# Revit family: FR_MEADRAIN_DM_CITY_Basic
name_source: partatom
category: Allgemeines Modell
revit_build: Autodesk Revit 2018 (Build: 20170223_1515(x64)
units: mm (PartAtom-declared; Revit-internal decimal feet)

## family parameters
Beim Laden mit Abzugskörper schneiden = Ja
Bemaßung runder Anschluss = Durchmesser verwenden
Gemeinsam genutzt = Nein
Kann Basisbauteil für Bewehrung sein = Nein
Raumberechnungspunkt = Nein
Teiletyp = Normal

## types (3) — shared parameters
B_diamétre intérieure_Manchon = 180 mm  [stored 0.590551 ft]
Bauelement = Caniveaux de surface
Beschreibung = System universel de drainage en béton polymère classes de charges jusqu'à D400
Def classe de charge_caniveau = D400
Diamétre extérieure_Manchon_element de revision = 200 mm  [stored 0.656168 ft]
Elément de drainage adapté pour = Pour une utilisation en milieu urbain
Fiche technique produit = https://www.mea-group.com
Fondation_largeur = 200 mm  [stored 0.656168 ft]
Grille = Gussrost
Hersteller = MEA Bautechnik GmbH business unit MEA Water Management
Hersteller und Typ- Ausschreibender gleichwertig = comme MEA Bautechnik GmbH, modèle MEADRAIN S
IfcDescription = System universel de drainage en béton polymère classes de charges jusqu'à D400
IfcExportAs = IfcWasteTerminalType
IfcExportType = USERDEFINED
Lien pour les produit = https://www.mea-group.com
Longeur_Manchon_Avaloir = 194 mm
Longeur_Manchon_element de revision = 180 mm  [stored 0.590551 ft]
MEA Consignes de pose = einschl. Fundament und Ummantelung
Matériau de construction, lit de pose/fondation = conformément aux dessins et à la description du produits
Modell = MEADRAIN DM
Plaque frontale_épaisseur = 3 mm  [stored 0.00984252 ft]
Techniques d'installation = Typ M
Type de élement de drainage = Beton
Typenkommentare = Pour une utilisation en milieu urbain
classe de charge de l'élement de drainage = D400
guid = cf6c1bd8-9bf4-4563-8c57-07955e2378ac
type de pente/ pourcentage de pente élement de drainage = Ohne Gefälle
Élement de construction ou de drainage = Entwässerungsrinne
zero-valued in all types: Avaloir_Fondation_visibilité

## per-type parameters (varying)
| type | B_H01 | B_largeur | Hauteur | Largeur nominal | Largeur_Caniveau | MEA- largeur nominal | Numéro d'article_Caniveau | hilfstype |
| DM CITY 1000 | 225 mm  [stored 0.738189 ft] | 133 mm  [stored 0.436352 ft] | 225 mm  [stored 0.738189 ft] | 100 mm  [stored 0.328084 ft] | 133 mm  [stored 0.436352 ft] | 1000 | 010712887 | 1 |
| DM CITY 1500 | 270 mm  [stored 0.885827 ft] | 183 mm | 270 mm  [stored 0.885827 ft] | 150 mm  [stored 0.492126 ft] | 183 mm | 1500 | 010712379 | 2 |
| DM CITY 2000 | 330 mm | 233 mm  [stored 0.764436 ft] | 330 mm | 200 mm  [stored 0.656168 ft] | 233 mm  [stored 0.764436 ft] | 2000 | 010712373 | 3 |

note: [stored X ft] marks values corroborated as IEEE doubles in the binary element streams (Revit-internal decimal feet)
